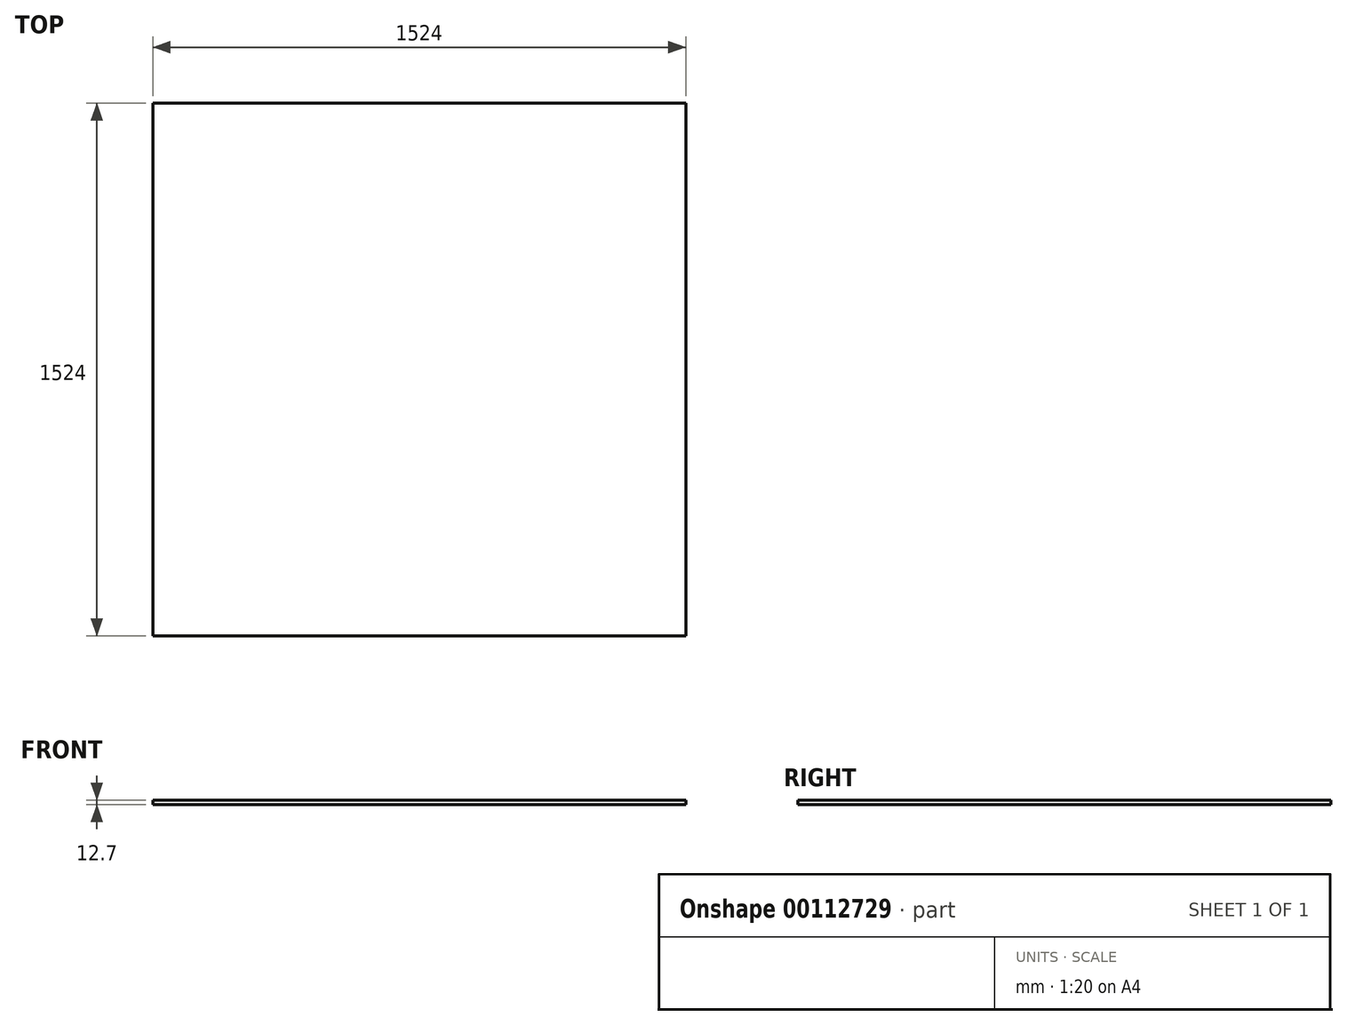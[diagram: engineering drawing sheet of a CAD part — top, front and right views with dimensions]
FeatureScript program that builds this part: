
annotation { "Feature Type Name" : "Feature", "Feature Type Description" : "" }
export const myFeature = defineFeature(function(context is Context, id is Id, definition is map)
    precondition{}
    {
        {
            var Q0;
            Q0=qCreatedBy(makeId("Top.planeOp"),FACE);
            var sketch = newSketch(context, id + "F0", { "sketchPlane" : qUnion([Q0])});
            skLineSegment(sketch, "E0.bottom", {"start": v(762, -762) * mm, "end": v(-762, -762) * mm});
            skLineSegment(sketch, "E0.top", {"start": v(762, 762) * mm, "end": v(-762, 762) * mm});
            skLineSegment(sketch, "E0.left", {"start": v(762, -762) * mm, "end": v(762, 762) * mm});
            skLineSegment(sketch, "E0.right", {"start": v(-762, -762) * mm, "end": v(-762, 762) * mm});
            skPoint(sketch, "E0.middle", {"position": v(0, 0) * mm});
            skSolve(sketch);
        }
        {
            var Q0;
            Q0=makeQuery(id+"F0.imprint","IMPRINT",FACE,{"disambiguationData":[TD([[makeQuery(id+"F0.imprint","IMPRINT",EDGE,{"derivedFrom":sQuery(id+"F0.wireOp",EDGE,"E0.bottom")}),-1.0]])]});
            extrude(context, id + "F1", {"entities" : qUnion([Q0]), "depth" : 12.7 * mm});
        }
    });
